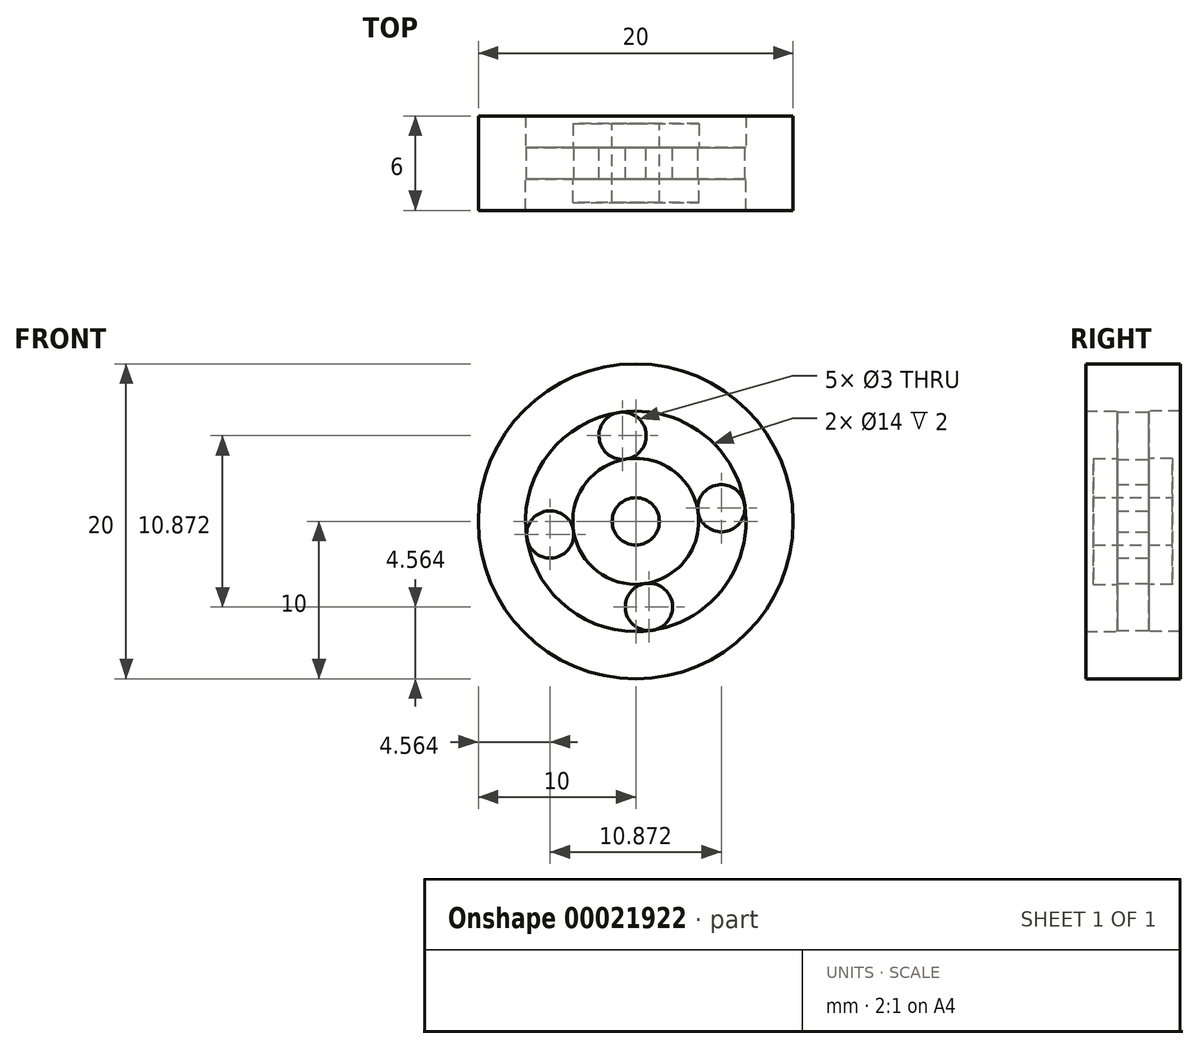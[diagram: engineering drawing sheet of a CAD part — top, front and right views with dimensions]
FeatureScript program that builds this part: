
annotation { "Feature Type Name" : "Feature", "Feature Type Description" : "" }
export const myFeature = defineFeature(function(context is Context, id is Id, definition is map)
    precondition{}
    {
        {
            var Q0;
            Q0=qCreatedBy(makeId("Front.planeOp"),FACE);
            var sketch = newSketch(context, id + "F0", { "sketchPlane" : qUnion([Q0])});
            skCircle(sketch, "E0", {"center": v(0, 0) * mm, "radius": 10 * mm});
            skCircle(sketch, "E1", {"center": v(0, 0) * mm, "radius": 1.5 * mm});
            skCircle(sketch, "E2", {"center": v(0, 0) * mm, "radius": 7 * mm});
            skCircle(sketch, "E3", {"center": v(0, 0) * mm, "radius": 4 * mm});
            skCircle(sketch, "E4", {"center": v(-0.84, 5.44) * mm, "radius": 1.5 * mm});
            skPoint(sketch, "E5.orphan", {"position": v(-1.06, 6.92) * mm});
            skPoint(sketch, "E6.trimOffspring.start.orphan", {"position": v(-0.6, 3.95) * mm});
            skCircle(sketch, "E7.1.0", {"center": v(-5.44, -0.84) * mm, "radius": 1.5 * mm});
            skCircle(sketch, "E7.2.0", {"center": v(0.84, -5.44) * mm, "radius": 1.5 * mm});
            skCircle(sketch, "E7.3.0", {"center": v(5.44, 0.84) * mm, "radius": 1.5 * mm});
            skSolve(sketch);
        }
        {
            var Q0;
            Q0=makeQuery(id+"F0.imprint","IMPRINT",FACE,{"disambiguationData":[TD([[makeQuery(id+"F0.imprint","IMPRINT",EDGE,{"derivedFrom":sQuery(id+"F0.wireOp",EDGE,"E0")}),1.0]])]});
            var Q1;
            {var subQ3=sQuery(id+"F0.wireOp",EDGE,"E2");var subQ5=sQuery(id+"F0.wireOp",EDGE,"E4");var subQ7=makeQuery(id+"F0.imprint","INTERSECT",VERTEX,{"derivedFrom":[subQ3,subQ5]});Q1=makeQuery(id+"F0.imprint","IMPRINT",FACE,{"disambiguationData":[TD([[makeQuery(id+"F0.imprint","IMPRINT",EDGE,{"disambiguationData":[TD([[subQ7,-1.0]])],"derivedFrom":subQ3}),1.0]])]});}
            var Q2;
            {var subQ3=sQuery(id+"F0.wireOp",EDGE,"E2");var subQ5=sQuery(id+"F0.wireOp",EDGE,"E4");var subQ7=makeQuery(id+"F0.imprint","INTERSECT",VERTEX,{"derivedFrom":[subQ3,subQ5]});Q2=makeQuery(id+"F0.imprint","IMPRINT",FACE,{"disambiguationData":[TD([[makeQuery(id+"F0.imprint","IMPRINT",EDGE,{"disambiguationData":[TD([[subQ7,1.0]])],"derivedFrom":subQ3}),1.0]])]});}
            var Q3;
            {var subQ0=sQuery(id+"F0.wireOp",EDGE,"E7.3.0");var subQ3=sQuery(id+"F0.wireOp",EDGE,"E2");var subQ4=makeQuery(id+"F0.imprint","INTERSECT",VERTEX,{"derivedFrom":[subQ3,subQ0]});Q3=makeQuery(id+"F0.imprint","IMPRINT",FACE,{"disambiguationData":[TD([[makeQuery(id+"F0.imprint","IMPRINT",EDGE,{"disambiguationData":[TD([[subQ4,1.0]])],"derivedFrom":subQ3}),1.0]])]});}
            var Q4;
            {var subQ0=sQuery(id+"F0.wireOp",EDGE,"E7.1.0");var subQ3=sQuery(id+"F0.wireOp",EDGE,"E2");var subQ4=makeQuery(id+"F0.imprint","INTERSECT",VERTEX,{"derivedFrom":[subQ3,subQ0]});Q4=makeQuery(id+"F0.imprint","IMPRINT",FACE,{"disambiguationData":[TD([[makeQuery(id+"F0.imprint","IMPRINT",EDGE,{"disambiguationData":[TD([[subQ4,-1.0]])],"derivedFrom":subQ3}),1.0]])]});}
            var Q5;
            Q5=makeQuery(id+"F0.imprint","IMPRINT",FACE,{"disambiguationData":[TD([[makeQuery(id+"F0.imprint","IMPRINT",EDGE,{"derivedFrom":sQuery(id+"F0.wireOp",EDGE,"E1")}),-1.0]])]});
            extrude(context, id + "F1", {"entities" : qUnion([Q0, Q1, Q2, Q3, Q4, Q5]), "endBound" : BoundingType.SYMMETRIC, "depth" : 2 * mm});
        }
        {
            var Q0;
            Q0=makeQuery(id+"F1.opExtrude","CAP_FACE",FACE,{"disambiguationData":[OSD([sQuery(id+"F0.wireOp",EDGE,"E0"),sQuery(id+"F0.wireOp",EDGE,"E1"),sQuery(id+"F0.wireOp",EDGE,"E4"),sQuery(id+"F0.wireOp",EDGE,"E7.1.0"),sQuery(id+"F0.wireOp",EDGE,"E7.2.0"),sQuery(id+"F0.wireOp",EDGE,"E7.3.0")])],"isStart":false});
            var sketch = newSketch(context, id + "F2", { "sketchPlane" : qUnion([Q0])});
            skCircle(sketch, "E8", {"center": v(0, 0) * mm, "radius": 7 * mm});
            skCircle(sketch, "E9", {"center": v(0, 0) * mm, "radius": 10 * mm});
            skSolve(sketch);
        }
        {
            var Q0;
            Q0=makeQuery(id+"F2.imprint","IMPRINT",FACE,{"disambiguationData":[TD([[makeQuery(id+"F2.imprint","IMPRINT",EDGE,{"derivedFrom":sQuery(id+"F2.wireOp",EDGE,"E9")}),1.0]])]});
            extrude(context, id + "F3", {"entities" : qUnion([Q0]), "operationType" : NewBodyOperationType.ADD, "depth" : 2 * mm});
        }
        {
            var Q0;
            Q0=makeQuery(id+"F1.opExtrude","CAP_FACE",FACE,{"disambiguationData":[OSD([sQuery(id+"F0.wireOp",EDGE,"E0"),sQuery(id+"F0.wireOp",EDGE,"E1"),sQuery(id+"F0.wireOp",EDGE,"E4"),sQuery(id+"F0.wireOp",EDGE,"E7.1.0"),sQuery(id+"F0.wireOp",EDGE,"E7.2.0"),sQuery(id+"F0.wireOp",EDGE,"E7.3.0")])],"isStart":true});
            var sketch = newSketch(context, id + "F4", { "sketchPlane" : qUnion([Q0])});
            skCircle(sketch, "E10", {"center": v(0, 0) * mm, "radius": 7 * mm});
            skCircle(sketch, "E11", {"center": v(0, 0) * mm, "radius": 10 * mm});
            skCircle(sketch, "E12", {"center": v(0, 0) * mm, "radius": 4 * mm});
            skSolve(sketch);
        }
        {
            var Q0;
            Q0=makeQuery(id+"F4.imprint","IMPRINT",FACE,{"disambiguationData":[TD([[makeQuery(id+"F4.imprint","IMPRINT",EDGE,{"derivedFrom":sQuery(id+"F4.wireOp",EDGE,"E11")}),-1.0]])]});
            extrude(context, id + "F5", {"entities" : qUnion([Q0]), "operationType" : NewBodyOperationType.ADD, "depth" : 2 * mm});
        }
        {
            var Q0;
            Q0=makeQuery(id+"F1.opExtrude","CAP_FACE",FACE,{"disambiguationData":[OSD([sQuery(id+"F0.wireOp",EDGE,"E0"),sQuery(id+"F0.wireOp",EDGE,"E1"),sQuery(id+"F0.wireOp",EDGE,"E4"),sQuery(id+"F0.wireOp",EDGE,"E7.1.0"),sQuery(id+"F0.wireOp",EDGE,"E7.2.0"),sQuery(id+"F0.wireOp",EDGE,"E7.3.0")])],"isStart":true});
            var sketch = newSketch(context, id + "F6", { "sketchPlane" : qUnion([Q0])});
            skCircle(sketch, "E13", {"center": v(0, 0) * mm, "radius": 4 * mm});
            skCircle(sketch, "E14", {"center": v(0, 0) * mm, "radius": 1.5 * mm});
            skSolve(sketch);
        }
        {
            var Q0;
            Q0=makeQuery(id+"F6.imprint","IMPRINT",FACE,{"disambiguationData":[TD([[makeQuery(id+"F6.imprint","IMPRINT",EDGE,{"derivedFrom":sQuery(id+"F6.wireOp",EDGE,"E14")}),1.0]])]});
            extrude(context, id + "F7", {"entities" : qUnion([Q0]), "operationType" : NewBodyOperationType.ADD, "depth" : 1.5 * mm});
        }
        {
            var Q0;
            Q0=makeQuery(id+"F1.opExtrude","CAP_FACE",FACE,{"disambiguationData":[OSD([sQuery(id+"F0.wireOp",EDGE,"E0"),sQuery(id+"F0.wireOp",EDGE,"E1"),sQuery(id+"F0.wireOp",EDGE,"E4"),sQuery(id+"F0.wireOp",EDGE,"E7.1.0"),sQuery(id+"F0.wireOp",EDGE,"E7.2.0"),sQuery(id+"F0.wireOp",EDGE,"E7.3.0")])],"isStart":false});
            var sketch = newSketch(context, id + "F8", { "sketchPlane" : qUnion([Q0])});
            skCircle(sketch, "E15", {"center": v(0, 0) * mm, "radius": 4 * mm});
            skCircle(sketch, "E16", {"center": v(0, 0) * mm, "radius": 1.5 * mm});
            skSolve(sketch);
        }
        {
            var Q0;
            Q0=makeQuery(id+"F8.imprint","IMPRINT",FACE,{"disambiguationData":[TD([[makeQuery(id+"F8.imprint","IMPRINT",EDGE,{"derivedFrom":sQuery(id+"F8.wireOp",EDGE,"E16")}),-1.0]])]});
            extrude(context, id + "F9", {"entities" : qUnion([Q0]), "operationType" : NewBodyOperationType.ADD, "depth" : 1.5 * mm});
        }
    });
